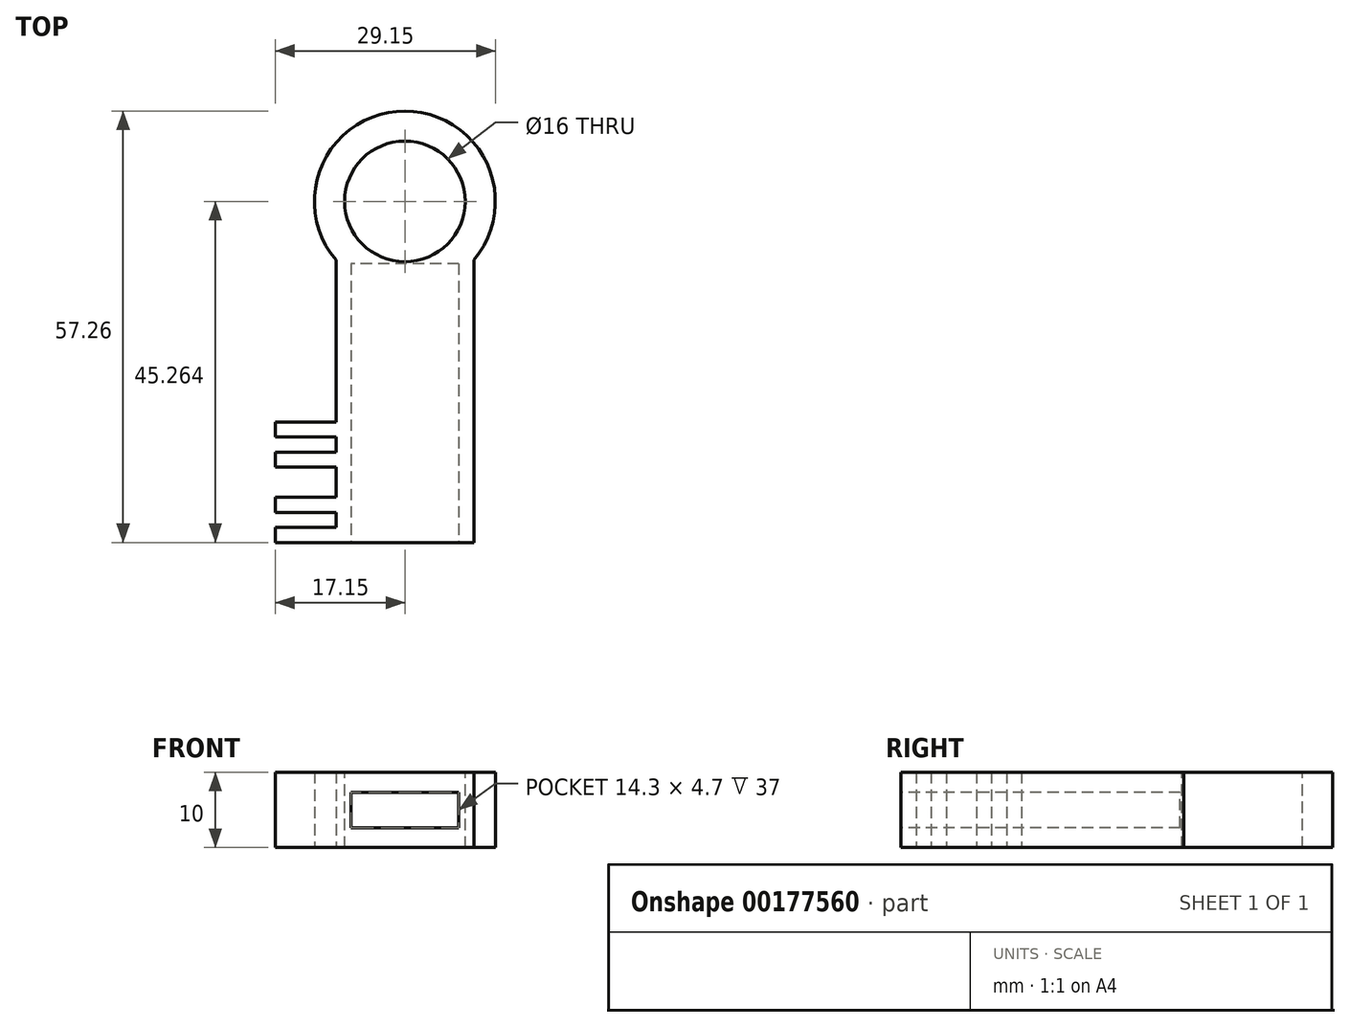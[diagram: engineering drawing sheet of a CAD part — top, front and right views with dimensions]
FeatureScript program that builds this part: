
annotation { "Feature Type Name" : "Feature", "Feature Type Description" : "" }
export const myFeature = defineFeature(function(context is Context, id is Id, definition is map)
    precondition{}
    {
        {
            var Q0;
            Q0=qCreatedBy(makeId("Top.planeOp"),FACE);
            var sketch = newSketch(context, id + "F0", { "sketchPlane" : qUnion([Q0])});
            skArc(sketch, "E0", {"start": v(9.15, 37.5) * mm, "mid": v(0, 57.26) * mm, "end": v(-9.15, 37.5) * mm});
            skLineSegment(sketch, "E1", {"start": v(-9.15, 37.5) * mm, "end": v(-9.15, 0) * mm});
            skLineSegment(sketch, "E2", {"start": v(-9.15, 0) * mm, "end": v(9.15, 0) * mm});
            skLineSegment(sketch, "E3", {"start": v(9.15, 0) * mm, "end": v(9.15, 37.5) * mm});
            skLineSegment(sketch, "E4", {"start": v(0, -42.6) * mm, "end": v(0, 118.76) * mm, "construction": true});
            skSolve(sketch);
        }
        {
            var Q0;
            Q0=makeQuery(id+"F0.imprint","IMPRINT",FACE,{"disambiguationData":[TD([[makeQuery(id+"F0.imprint","IMPRINT",EDGE,{"derivedFrom":sQuery(id+"F0.wireOp",EDGE,"E0")}),1.0]])]});
            extrude(context, id + "F1", {"entities" : qUnion([Q0]), "depth" : 10 * mm});
        }
        {
            var Q0;
            Q0=makeQuery(id+"F1.opExtrude","CAP_FACE",FACE,{"disambiguationData":[OSD([sQuery(id+"F0.wireOp",EDGE,"E0"),sQuery(id+"F0.wireOp",EDGE,"E1"),sQuery(id+"F0.wireOp",EDGE,"E2"),sQuery(id+"F0.wireOp",EDGE,"E3")])],"isStart":false});
            var sketch = newSketch(context, id + "F2", { "sketchPlane" : qUnion([Q0])});
            skCircle(sketch, "E5", {"center": v(0, 45.26) * mm, "radius": 8 * mm});
            skSolve(sketch);
        }
        {
            var Q0;
            Q0 = qSketchRegion(id + "F2", true);
            extrude(context, id + "F3", {"entities" : qUnion([Q0]), "operationType" : NewBodyOperationType.REMOVE, "endBound" : BoundingType.THROUGH_ALL, "oppositeDirection" : true, "depth" : 25 * mm});
        }
        {
            var Q0;
            Q0=makeQuery(id+"F1.opExtrude","SWEPT_FACE",FACE,{"disambiguationData":[OSD([sQuery(id+"F0.wireOp",EDGE,"E2")])]});
            var sketch = newSketch(context, id + "F4", { "sketchPlane" : qUnion([Q0])});
            skLineSegment(sketch, "E6.bottom", {"start": v(7.15, 2.65) * mm, "end": v(-7.15, 2.65) * mm});
            skLineSegment(sketch, "E6.top", {"start": v(7.15, 7.35) * mm, "end": v(-7.15, 7.35) * mm});
            skLineSegment(sketch, "E6.left", {"start": v(7.15, 2.65) * mm, "end": v(7.15, 7.35) * mm});
            skLineSegment(sketch, "E6.right", {"start": v(-7.15, 2.65) * mm, "end": v(-7.15, 7.35) * mm});
            skLineSegment(sketch, "E7", {"start": v(20.35, 5) * mm, "end": v(-44.3, 5) * mm, "construction": true});
            skSolve(sketch);
        }
        {
            var Q0;
            Q0 = qSketchRegion(id + "F4", true);
            extrude(context, id + "F5", {"entities" : qUnion([Q0]), "operationType" : NewBodyOperationType.REMOVE, "oppositeDirection" : true, "depth" : 37 * mm});
        }
        {
            var Q0;
            Q0=makeQuery(id+"F1.opExtrude","SWEPT_FACE",FACE,{"disambiguationData":[OSD([sQuery(id+"F0.wireOp",EDGE,"E1")])]});
            var sketch = newSketch(context, id + "F6", { "sketchPlane" : qUnion([Q0])});
            skLineSegment(sketch, "E8.bottom", {"start": v(0, 10) * mm, "end": v(-2, 10) * mm});
            skLineSegment(sketch, "E8.top", {"start": v(0, 0) * mm, "end": v(-2, 0) * mm});
            skLineSegment(sketch, "E8.left", {"start": v(0, 10) * mm, "end": v(0, 0) * mm});
            skLineSegment(sketch, "E8.right", {"start": v(-2, 10) * mm, "end": v(-2, 0) * mm});
            skLineSegment(sketch, "E9.bottom", {"start": v(-4, 10) * mm, "end": v(-6, 10) * mm});
            skLineSegment(sketch, "E9.top", {"start": v(-4, 0) * mm, "end": v(-6, 0) * mm});
            skLineSegment(sketch, "E9.left", {"start": v(-4, 10) * mm, "end": v(-4, 0) * mm});
            skLineSegment(sketch, "E9.right", {"start": v(-6, 10) * mm, "end": v(-6, 0) * mm});
            skLineSegment(sketch, "E10.bottom", {"start": v(-10, 10) * mm, "end": v(-12, 10) * mm});
            skLineSegment(sketch, "E10.top", {"start": v(-10, 0) * mm, "end": v(-12, 0) * mm});
            skLineSegment(sketch, "E10.left", {"start": v(-10, 10) * mm, "end": v(-10, 0) * mm});
            skLineSegment(sketch, "E10.right", {"start": v(-12, 10) * mm, "end": v(-12, 0) * mm});
            skLineSegment(sketch, "E11.bottom", {"start": v(-14, 10) * mm, "end": v(-16, 10) * mm});
            skLineSegment(sketch, "E11.top", {"start": v(-14, 0) * mm, "end": v(-16, 0) * mm});
            skLineSegment(sketch, "E11.left", {"start": v(-14, 10) * mm, "end": v(-14, 0) * mm});
            skLineSegment(sketch, "E11.right", {"start": v(-16, 10) * mm, "end": v(-16, 0) * mm});
            skSolve(sketch);
        }
        {
            var Q0;
            Q0 = qSketchRegion(id + "F6", true);
            extrude(context, id + "F7", {"entities" : qUnion([Q0]), "operationType" : NewBodyOperationType.ADD, "depth" : 8 * mm});
        }
    });
